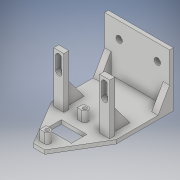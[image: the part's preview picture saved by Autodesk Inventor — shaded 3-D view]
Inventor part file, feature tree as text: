
AUTODESK INVENTOR PART (.ipt)
format: ipt  version: 2019 (Build 230136000, 136)  size: 352,768 bytes
history: native  units: in
note: dims shown in document units (in); Inventor stores cm internally (conversion verified against a paired STEP export)
features: sketch x21, extrude x10, loft x5, hole x3, plane x1
ambient origin geometry x8: Origin, YZ Plane, XZ Plane, XY Plane, X Axis, Y Axis, Z Axis, Center Point
bodies: Solid1 (feature_tree)
feature tree (40):
  extrude  "Extrusion1"  Depth=1.5748in
  extrude  "Extrusion2"  Depth=0.1969in
  loft  "Loft1"
  loft  "Loft2"
  extrude  "Extrusion3"  Depth=0.1181in TaperAngle=0.0deg
  loft  "Loft3"
  loft  "Loft4"
  plane  "Work Plane1"
  loft  "Loft5"
  sketch  "Sketch14"  dims[d36=0.315in d37=0.0787in]
  extrude  "Extrusion4"  TaperAngle=0.0deg  [1 undecoded]
  hole  "Hole1"  [1 undecoded]
  hole  "Hole2"  [1 undecoded]
  extrude  "Extrusion5"  Depth=0.6299in
  sketch  "Sketch17"  dims[d43=1.5748in d44=0.0in d46=0.1969in]
  extrude  "Extrusion6"  TaperAngle=0.0deg  [1 undecoded]
  hole  "Hole3"  [1 undecoded]
  extrude  "Extrusion7"  Depth=0.315in
  extrude  "Extrusion8"  Depth=0.315in
  extrude  "Extrusion9"  Depth=0.1969in
  extrude  "Extrusion10"  Depth=0.1969in
  sketch  "Sketch1"  dims[d0=2.0079in d1=1.5748in]
  sketch  "Sketch2"  dims[d2=2.0079in d5=0.1969in]
  sketch  "Sketch3"  dims[d7=0.1969in d8=0.1181in d9=0.0in]
  sketch  "Sketch4"  dims[d10=1.7717in d11=2.0079in]
  sketch  "Sketch5"  dims[d12=1.7717in d13=0.1181in d14=0.0in]
  sketch  "Sketch6"  dims[d15=0.3543in d16=0.1969in]
  sketch  "Sketch7"  dims[d17=0.3543in d18=0.6299in]
  sketch  "Sketch8"  dims[d19=0.1969in d20=0.6299in]
  sketch  "Sketch9"  dims[d21=0.0in d22=90.0deg d23=0.0in d24=90.0deg]
  sketch  "Sketch10"  dims[d25=0.3543in d26=0.1969in]
  sketch  "Sketch11"  dims[d27=0.3543in d28=0.6299in]
  sketch  "Sketch12"  dims[d29=0.1969in d30=0.6299in]
  sketch  "Sketch13"  dims[d31=0.0in d32=90.0deg d33=0.0in d34=90.0deg]
  sketch  "Sketch15"  dims[d38=0.315in d40=0.315in]
  sketch  "Sketch16"  dims[d41=0.0787in d42=0.315in]
  sketch  "Sketch18"  dims[d47=0.5906in d48=0.1969in]
  sketch  "Sketch19"  dims[d49=0.7874in]
  sketch  "Sketch20"  dims[d50=0.1969in]
  sketch  "Sketch21"  dims[d51=0.7874in d52=0.0in d53=90.0deg d54=0.0in d55=90.0deg d56=0.1181in d57=0.5906in d58=0.1969in d59=0.5906in d60=0.7874in d61=0.1969in d62=0.7874in d63=0.0in d64=90.0deg d65=0.0in d66=90.0deg d67=1.378in d69=0.1181in d70=0.3543in d71=0.1181in d72=0.0in d73=90.0deg d74=0.0in d75=90.0deg d77=0.0984in d78=0.0984in d79=0.2362in d80=0.1969in d81=0.2362in d82=0.0984in d83=0.315in d84=0.0in d85=0.1181in d86=0.2362in d87=0.1575in d88=0.0787in d89=90.0deg d90=0.0984in d91=0.8108in d92=0.1181in d93=0.1181in d94=0.2362in d95=0.1575in d96=0.0787in d97=90.0deg d98=0.0984in d99=0.0in d103=0.4724in d104=0.7874in d105=0.1181in d106=0.0in d108=0.2362in d110=0.1969in d111=0.2362in d112=0.1969in d113=0.0984in d114=0.315in d115=0.0in d116=0.1181in d117=0.2362in d118=0.1575in d119=0.0787in d120=90.0deg d121=0.0984in d122=0.0in d125=0.5906in d126=0.1969in d127=0.5906in d128=0.0984in d129=0.0787in d130=0.0in d133=0.5906in d134=0.1969in d135=0.5906in d136=0.0984in d137=0.0787in d138=0.0in d139=0.0591in d140=0.0787in d141=0.1969in d142=0.5906in d143=0.1969in d144=0.0984in d145=0.0787in d146=0.0in d147=0.0591in d150=0.5906in d151=0.1969in d152=0.0984in d153=0.0787in d154=0.0in]
note: 5 required parameter values undecoded (feature->parameter linkage not recoverable at this tier; creation-order binding heuristic only, values carry confidence <= 0.55)
